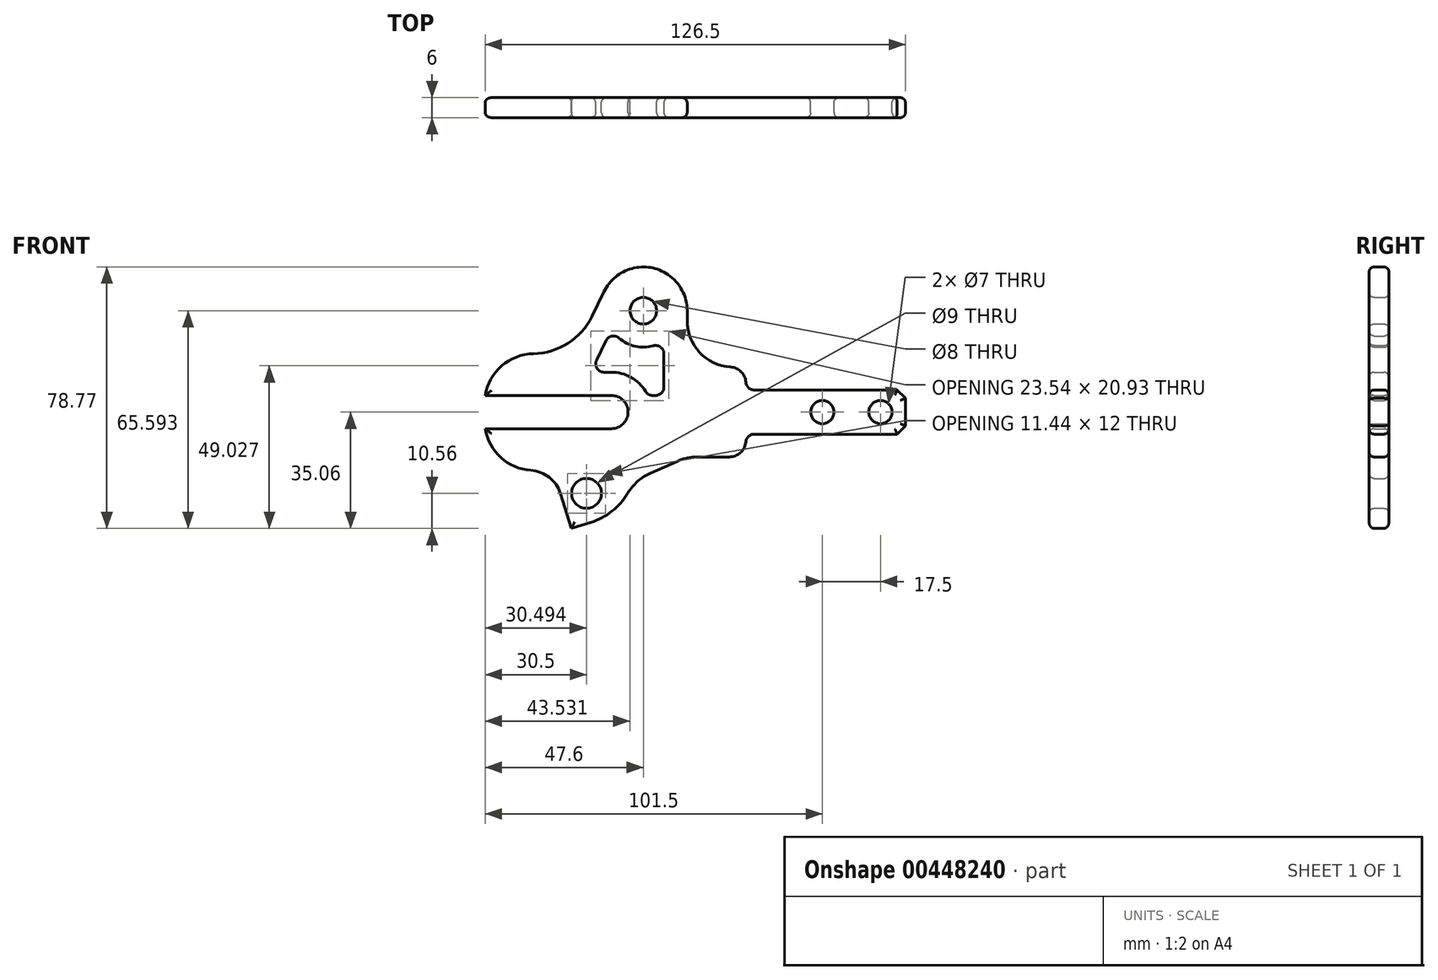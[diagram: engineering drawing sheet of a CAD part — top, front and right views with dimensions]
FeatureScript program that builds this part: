
annotation { "Feature Type Name" : "Feature", "Feature Type Description" : "" }
export const myFeature = defineFeature(function(context is Context, id is Id, definition is map)
    precondition{}
    {
        {
            var Q0;
            Q0=qCreatedBy(makeId("Front.planeOp"),FACE);
            var sketch = newSketch(context, id + "F0", { "sketchPlane" : qUnion([Q0])});
            skArc(sketch, "E0", {"start": v(0, -5) * mm, "mid": v(5, 0) * mm, "end": v(0, 5) * mm});
            skLineSegment(sketch, "E1", {"start": v(0, 5) * mm, "end": v(-38, 5) * mm});
            skLineSegment(sketch, "E2.MirrorCS", {"start": v(0, -5) * mm, "end": v(-38, -5) * mm});
            skLineSegment(sketch, "E3", {"start": v(-38, 5) * mm, "end": v(-38, 17.6) * mm});
            skLineSegment(sketch, "E4", {"start": v(-38, 17.6) * mm, "end": v(-11.3, 17.6) * mm});
            skLineSegment(sketch, "E5", {"start": v(-11.3, 17.6) * mm, "end": v(-2.24, 36.27) * mm});
            skLineSegment(sketch, "E6", {"start": v(17, 41.46) * mm, "end": v(17.04, 41.43) * mm});
            skLineSegment(sketch, "E7", {"start": v(22.8, 30.53) * mm, "end": v(22.8, 13.53) * mm});
            skLineSegment(sketch, "E8", {"start": v(22.8, 13.53) * mm, "end": v(40.5, 13.53) * mm});
            skLineSegment(sketch, "E9", {"start": v(40.5, 13.53) * mm, "end": v(40.5, 6.65) * mm});
            skLineSegment(sketch, "E10", {"start": v(40.5, 6.65) * mm, "end": v(88.5, 6.65) * mm});
            skLineSegment(sketch, "E11.MirrorCS", {"start": v(40.5, -6.65) * mm, "end": v(88.5, -6.65) * mm});
            skLineSegment(sketch, "E12.MirrorCS", {"start": v(40.5, -13.53) * mm, "end": v(40.5, -6.65) * mm});
            skLineSegment(sketch, "E13.MirrorCS", {"start": v(22.8, -13.53) * mm, "end": v(40.5, -13.53) * mm});
            skLineSegment(sketch, "E14", {"start": v(2.4, -30.53) * mm, "end": v(-12.05, -35.06) * mm});
            skLineSegment(sketch, "E15", {"start": v(-12.05, -35.06) * mm, "end": v(-17.52, -17.6) * mm});
            skLineSegment(sketch, "E16", {"start": v(-17.52, -17.6) * mm, "end": v(-38, -17.6) * mm});
            skLineSegment(sketch, "E17", {"start": v(-38, -17.6) * mm, "end": v(-38, -5) * mm});
            skLineSegment(sketch, "E18", {"start": v(88.5, 6.65) * mm, "end": v(88.5, -6.65) * mm});
            skCircle(sketch, "E19", {"center": v(-7.5, -24.5) * mm, "radius": 4.5 * mm});
            skCircle(sketch, "E20", {"center": v(81, 0) * mm, "radius": 3.5 * mm});
            skPoint(sketch, "E20.centerSnap0", {"position": v(88.5, 0) * mm});
            skCircle(sketch, "E21", {"center": v(63.5, 0) * mm, "radius": 3.5 * mm});
            skPoint(sketch, "E22.visualSharp", {"position": v(4.42, 49.99) * mm});
            skArc(sketch, "E22.filletArc", {"start": v(17.04, 41.43) * mm, "mid": v(6.22, 43.26) * mm, "end": v(-2.24, 36.27) * mm});
            skPoint(sketch, "E23.visualSharp", {"position": v(22.8, 37.53) * mm});
            skArc(sketch, "E23.filletArc", {"start": v(22.8, 30.53) * mm, "mid": v(21.26, 36.72) * mm, "end": v(17, 41.46) * mm});
            skCircle(sketch, "E24", {"center": v(9.6, 30.53) * mm, "radius": 4 * mm});
            skLineSegment(sketch, "E25", {"start": v(2.4, -30.53) * mm, "end": v(6, -20.92) * mm});
            skLineSegment(sketch, "E26", {"start": v(6, -20.92) * mm, "end": v(22.8, -13.53) * mm});
            skLineSegment(sketch, "E27.0", {"start": v(-6.24, 12) * mm, "end": v(0.08, 25.02) * mm});
            skLineSegment(sketch, "E28.0", {"start": v(15.8, 21.45) * mm, "end": v(15.8, 5) * mm});
            skLineSegment(sketch, "E29", {"start": v(-6.24, 12) * mm, "end": v(0, 12) * mm});
            skArc(sketch, "E30", {"start": v(0, 12) * mm, "mid": v(6.48, 10.1) * mm, "end": v(10.9, 5) * mm});
            skLineSegment(sketch, "E31", {"start": v(10.9, 5) * mm, "end": v(15.8, 5) * mm});
            skArc(sketch, "E32", {"start": v(0.08, 25.02) * mm, "mid": v(7.16, 19.8) * mm, "end": v(15.8, 21.45) * mm});
            skSolve(sketch);
        }
        {
            var Q0;
            Q0=makeQuery(id+"F0.imprint","IMPRINT",FACE,{"disambiguationData":[TD([[makeQuery(id+"F0.imprint","IMPRINT",EDGE,{"derivedFrom":sQuery(id+"F0.wireOp",EDGE,"E0")}),-1.0]])]});
            extrude(context, id + "F1", {"entities" : qUnion([Q0]), "endBound" : BoundingType.SYMMETRIC, "depth" : 6 * mm});
        }
        {
            var Q0;
            Q0=makeQuery(id+"F1.opExtrude","SWEPT_EDGE",EDGE,{"disambiguationData":[OSD([sQuery(id+"F0.wireOp",EDGE,"E3"),sQuery(id+"F0.wireOp",EDGE,"E4")])]});
            var Q1;
            Q1=makeQuery(id+"F1.opExtrude","SWEPT_EDGE",EDGE,{"disambiguationData":[OSD([sQuery(id+"F0.wireOp",EDGE,"E16"),sQuery(id+"F0.wireOp",EDGE,"E17")])]});
            fillet(context, id + "F2", {"entities" : qUnion([Q0, Q1]), "radius" : 15 * mm, "tangentPropagation" : true, "allowEdgeOverflow" : false});
        }
        {
            var Q0;
            Q0=makeQuery(id+"F1.opExtrude","SWEPT_EDGE",EDGE,{"disambiguationData":[OSD([sQuery(id+"F0.wireOp",EDGE,"E4"),sQuery(id+"F0.wireOp",EDGE,"E5")])]});
            fillet(context, id + "F3", {"entities" : qUnion([Q0]), "radius" : 20 * mm, "allowEdgeOverflow" : false});
        }
        {
            var Q0;
            Q0=makeQuery(id+"F1.opExtrude","SWEPT_EDGE",EDGE,{"disambiguationData":[OSD([sQuery(id+"F0.wireOp",EDGE,"E5"),sQuery(id+"F0.wireOp",EDGE,"E6")])]});
            var Q1;
            Q1=makeQuery(id+"F1.opExtrude","SWEPT_EDGE",EDGE,{"disambiguationData":[OSD([sQuery(id+"F0.wireOp",EDGE,"E6"),sQuery(id+"F0.wireOp",EDGE,"E7")])]});
            fillet(context, id + "F4", {"entities" : qUnion([Q0, Q1]), "radius" : 14 * mm, "tangentPropagation" : true, "allowEdgeOverflow" : false});
        }
        {
            var Q0;
            Q0=makeQuery(id+"F1.opExtrude","SWEPT_EDGE",EDGE,{"disambiguationData":[OSD([sQuery(id+"F0.wireOp",EDGE,"E12.MirrorCS"),sQuery(id+"F0.wireOp",EDGE,"E13.MirrorCS")])]});
            var Q1;
            Q1=makeQuery(id+"F1.opExtrude","SWEPT_EDGE",EDGE,{"disambiguationData":[OSD([sQuery(id+"F0.wireOp",EDGE,"E8"),sQuery(id+"F0.wireOp",EDGE,"E9")])]});
            fillet(context, id + "F5", {"entities" : qUnion([Q0, Q1]), "radius" : 5 * mm, "tangentPropagation" : true, "allowEdgeOverflow" : false});
        }
        {
            var Q0;
            Q0=makeQuery(id+"F1.opExtrude","SWEPT_EDGE",EDGE,{"disambiguationData":[OSD([sQuery(id+"F0.wireOp",EDGE,"E10"),sQuery(id+"F0.wireOp",EDGE,"E18")])]});
            var Q1;
            Q1=makeQuery(id+"F1.opExtrude","SWEPT_EDGE",EDGE,{"disambiguationData":[OSD([sQuery(id+"F0.wireOp",EDGE,"E11.MirrorCS"),sQuery(id+"F0.wireOp",EDGE,"E18")])]});
            chamfer(context, id + "F6", {"entities" : qUnion([Q0, Q1]), "width" : 2.5 * mm, "tangentPropagation" : true});
        }
        {
            var Q0;
            Q0=makeQuery(id+"F1.opExtrude","SWEPT_EDGE",EDGE,{"disambiguationData":[OSD([sQuery(id+"F0.wireOp",EDGE,"E13.MirrorCS"),sQuery(id+"F0.wireOp",EDGE,"E26")])]});
            var Q1;
            Q1=makeQuery(id+"F1.opExtrude","SWEPT_EDGE",EDGE,{"disambiguationData":[OSD([sQuery(id+"F0.wireOp",EDGE,"E25"),sQuery(id+"F0.wireOp",EDGE,"E26")])]});
            fillet(context, id + "F7", {"entities" : qUnion([Q0, Q1]), "radius" : 15 * mm, "tangentPropagation" : true, "allowEdgeOverflow" : false});
        }
        {
            var Q0;
            Q0=makeQuery(id+"F1.opExtrude","SWEPT_EDGE",EDGE,{"disambiguationData":[OSD([sQuery(id+"F0.wireOp",EDGE,"E14"),sQuery(id+"F0.wireOp",EDGE,"E25")])]});
            fillet(context, id + "F8", {"entities" : qUnion([Q0]), "radius" : 20 * mm, "tangentPropagation" : true, "allowEdgeOverflow" : false});
        }
        {
            var Q0;
            Q0=makeQuery(id+"F1.opExtrude","SWEPT_EDGE",EDGE,{"disambiguationData":[OSD([sQuery(id+"F0.wireOp",EDGE,"E15"),sQuery(id+"F0.wireOp",EDGE,"E16")])]});
            fillet(context, id + "F9", {"entities" : qUnion([Q0]), "radius" : 10 * mm, "tangentPropagation" : true, "allowEdgeOverflow" : false});
        }
        {
            var Q0;
            Q0=makeQuery(id+"F1.opExtrude","SWEPT_EDGE",EDGE,{"disambiguationData":[OSD([sQuery(id+"F0.wireOp",EDGE,"E9"),sQuery(id+"F0.wireOp",EDGE,"E10")])]});
            var Q1;
            Q1=makeQuery(id+"F1.opExtrude","SWEPT_EDGE",EDGE,{"disambiguationData":[OSD([sQuery(id+"F0.wireOp",EDGE,"E11.MirrorCS"),sQuery(id+"F0.wireOp",EDGE,"E12.MirrorCS")])]});
            fillet(context, id + "F10", {"entities" : qUnion([Q0, Q1]), "radius" : 2.5 * mm, "tangentPropagation" : true, "allowEdgeOverflow" : false});
        }
        {
            var Q0;
            Q0=makeQuery(id+"F1.opExtrude","SWEPT_EDGE",EDGE,{"disambiguationData":[OSD([sQuery(id+"F0.wireOp",EDGE,"E27.0"),sQuery(id+"F0.wireOp",EDGE,"E32")])]});
            var Q1;
            Q1=makeQuery(id+"F1.opExtrude","SWEPT_EDGE",EDGE,{"disambiguationData":[OSD([sQuery(id+"F0.wireOp",EDGE,"E28.0"),sQuery(id+"F0.wireOp",EDGE,"E32")])]});
            var Q2;
            Q2=makeQuery(id+"F1.opExtrude","SWEPT_EDGE",EDGE,{"disambiguationData":[OSD([sQuery(id+"F0.wireOp",EDGE,"E27.0"),sQuery(id+"F0.wireOp",EDGE,"E29")])]});
            var Q3;
            Q3=makeQuery(id+"F1.opExtrude","SWEPT_EDGE",EDGE,{"disambiguationData":[OSD([sQuery(id+"F0.wireOp",EDGE,"E30"),sQuery(id+"F0.wireOp",EDGE,"E31")])]});
            var Q4;
            Q4=makeQuery(id+"F1.opExtrude","SWEPT_EDGE",EDGE,{"disambiguationData":[OSD([sQuery(id+"F0.wireOp",EDGE,"E28.0"),sQuery(id+"F0.wireOp",EDGE,"E31")])]});
            fillet(context, id + "F11", {"entities" : qUnion([Q0, Q1, Q2, Q3, Q4]), "radius" : 2.5 * mm, "tangentPropagation" : true, "allowEdgeOverflow" : false});
        }
        {
            var Q0;
            Q0=makeQuery(id+"F1.opExtrude","CAP_FACE",FACE,{"disambiguationData":[OSD([sQuery(id+"F0.wireOp",EDGE,"E0"),sQuery(id+"F0.wireOp",EDGE,"E1"),sQuery(id+"F0.wireOp",EDGE,"E2.MirrorCS"),sQuery(id+"F0.wireOp",EDGE,"E3"),sQuery(id+"F0.wireOp",EDGE,"E4"),sQuery(id+"F0.wireOp",EDGE,"E5"),sQuery(id+"F0.wireOp",EDGE,"E7"),sQuery(id+"F0.wireOp",EDGE,"E8"),sQuery(id+"F0.wireOp",EDGE,"E9"),sQuery(id+"F0.wireOp",EDGE,"E10"),sQuery(id+"F0.wireOp",EDGE,"E11.MirrorCS"),sQuery(id+"F0.wireOp",EDGE,"E12.MirrorCS"),sQuery(id+"F0.wireOp",EDGE,"E13.MirrorCS"),sQuery(id+"F0.wireOp",EDGE,"E14"),sQuery(id+"F0.wireOp",EDGE,"E15"),sQuery(id+"F0.wireOp",EDGE,"E16"),sQuery(id+"F0.wireOp",EDGE,"E17"),sQuery(id+"F0.wireOp",EDGE,"E18"),sQuery(id+"F0.wireOp",EDGE,"E19"),sQuery(id+"F0.wireOp",EDGE,"E20"),sQuery(id+"F0.wireOp",EDGE,"E21"),sQuery(id+"F0.wireOp",EDGE,"E22.filletArc"),sQuery(id+"F0.wireOp",EDGE,"E23.filletArc"),sQuery(id+"F0.wireOp",EDGE,"E24"),sQuery(id+"F0.wireOp",EDGE,"E25"),sQuery(id+"F0.wireOp",EDGE,"E26"),sQuery(id+"F0.wireOp",EDGE,"E27.0"),sQuery(id+"F0.wireOp",EDGE,"E28.0"),sQuery(id+"F0.wireOp",EDGE,"E29"),sQuery(id+"F0.wireOp",EDGE,"E30"),sQuery(id+"F0.wireOp",EDGE,"E31"),sQuery(id+"F0.wireOp",EDGE,"E32")])],"isStart":false});
            var Q1;
            Q1=makeQuery(id+"F1.opExtrude","CAP_FACE",FACE,{"disambiguationData":[OSD([sQuery(id+"F0.wireOp",EDGE,"E0"),sQuery(id+"F0.wireOp",EDGE,"E1"),sQuery(id+"F0.wireOp",EDGE,"E2.MirrorCS"),sQuery(id+"F0.wireOp",EDGE,"E3"),sQuery(id+"F0.wireOp",EDGE,"E4"),sQuery(id+"F0.wireOp",EDGE,"E5"),sQuery(id+"F0.wireOp",EDGE,"E7"),sQuery(id+"F0.wireOp",EDGE,"E8"),sQuery(id+"F0.wireOp",EDGE,"E9"),sQuery(id+"F0.wireOp",EDGE,"E10"),sQuery(id+"F0.wireOp",EDGE,"E11.MirrorCS"),sQuery(id+"F0.wireOp",EDGE,"E12.MirrorCS"),sQuery(id+"F0.wireOp",EDGE,"E13.MirrorCS"),sQuery(id+"F0.wireOp",EDGE,"E14"),sQuery(id+"F0.wireOp",EDGE,"E15"),sQuery(id+"F0.wireOp",EDGE,"E16"),sQuery(id+"F0.wireOp",EDGE,"E17"),sQuery(id+"F0.wireOp",EDGE,"E18"),sQuery(id+"F0.wireOp",EDGE,"E19"),sQuery(id+"F0.wireOp",EDGE,"E20"),sQuery(id+"F0.wireOp",EDGE,"E21"),sQuery(id+"F0.wireOp",EDGE,"E22.filletArc"),sQuery(id+"F0.wireOp",EDGE,"E23.filletArc"),sQuery(id+"F0.wireOp",EDGE,"E24"),sQuery(id+"F0.wireOp",EDGE,"E25"),sQuery(id+"F0.wireOp",EDGE,"E26"),sQuery(id+"F0.wireOp",EDGE,"E27.0"),sQuery(id+"F0.wireOp",EDGE,"E28.0"),sQuery(id+"F0.wireOp",EDGE,"E29"),sQuery(id+"F0.wireOp",EDGE,"E30"),sQuery(id+"F0.wireOp",EDGE,"E31"),sQuery(id+"F0.wireOp",EDGE,"E32")])],"isStart":true});
            fillet(context, id + "F12", {"entities" : qUnion([Q0, Q1]), "radius" : 1.5 * mm, "tangentPropagation" : true, "allowEdgeOverflow" : false});
        }
    });
